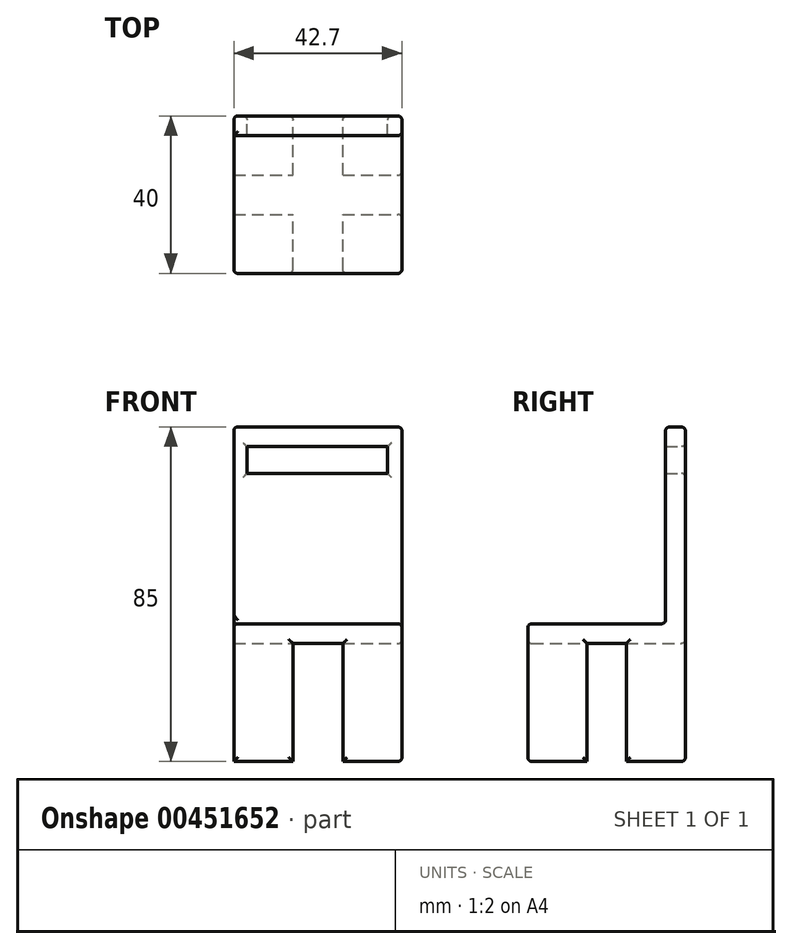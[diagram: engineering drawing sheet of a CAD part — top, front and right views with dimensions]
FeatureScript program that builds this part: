
annotation { "Feature Type Name" : "Feature", "Feature Type Description" : "" }
export const myFeature = defineFeature(function(context is Context, id is Id, definition is map)
    precondition{}
    {
        {
            var Q0;
            Q0=qCreatedBy(makeId("Top.planeOp"),FACE);
            var sketch = newSketch(context, id + "F0", { "sketchPlane" : qUnion([Q0])});
            skLineSegment(sketch, "E0.bottom", {"start": v(10, 10) * mm, "end": v(25, 10) * mm});
            skLineSegment(sketch, "E0.top", {"start": v(10, 25) * mm, "end": v(25, 25) * mm});
            skLineSegment(sketch, "E0.left", {"start": v(10, 10) * mm, "end": v(10, 25) * mm});
            skLineSegment(sketch, "E0.right", {"start": v(25, 10) * mm, "end": v(25, 25) * mm});
            skLineSegment(sketch, "E1.0.1.0", {"start": v(10, 50) * mm, "end": v(25, 50) * mm});
            skLineSegment(sketch, "E1.0.1.1", {"start": v(10, 35) * mm, "end": v(10, 50) * mm});
            skLineSegment(sketch, "E1.0.1.2", {"start": v(10, 35) * mm, "end": v(25, 35) * mm});
            skLineSegment(sketch, "E1.0.1.3", {"start": v(25, 35) * mm, "end": v(25, 50) * mm});
            skLineSegment(sketch, "E1.1.0.0", {"start": v(37.7, 25) * mm, "end": v(52.7, 25) * mm});
            skLineSegment(sketch, "E1.1.0.1", {"start": v(37.7, 10) * mm, "end": v(37.7, 25) * mm});
            skLineSegment(sketch, "E1.1.0.2", {"start": v(37.7, 10) * mm, "end": v(52.7, 10) * mm});
            skLineSegment(sketch, "E1.1.0.3", {"start": v(52.7, 10) * mm, "end": v(52.7, 25) * mm});
            skLineSegment(sketch, "E1.1.1.0", {"start": v(37.7, 50) * mm, "end": v(52.7, 50) * mm});
            skLineSegment(sketch, "E1.1.1.1", {"start": v(37.7, 35) * mm, "end": v(37.7, 50) * mm});
            skLineSegment(sketch, "E1.1.1.2", {"start": v(37.7, 35) * mm, "end": v(52.7, 35) * mm});
            skLineSegment(sketch, "E1.1.1.3", {"start": v(52.7, 35) * mm, "end": v(52.7, 50) * mm});
            skLineSegment(sketch, "E1.direction1", {"start": v(10, 25) * mm, "end": v(37.7, 25) * mm, "construction": true});
            skLineSegment(sketch, "E1.direction2", {"start": v(10, 25) * mm, "end": v(10, 50) * mm, "construction": true});
            skSolve(sketch);
        }
        {
            var Q0;
            Q0 = qSketchRegion(id + "F0", true);
            extrude(context, id + "F1", {"entities" : qUnion([Q0]), "depth" : 30 * mm});
        }
        {
            var Q0;
            Q0=makeQuery(id+"F1.opExtrude","CAP_FACE",FACE,{"disambiguationData":[OSD([sQuery(id+"F0.wireOp",EDGE,"E1.0.1.0"),sQuery(id+"F0.wireOp",EDGE,"E1.0.1.1"),sQuery(id+"F0.wireOp",EDGE,"E1.0.1.2"),sQuery(id+"F0.wireOp",EDGE,"E1.0.1.3")])],"isStart":false});
            var sketch = newSketch(context, id + "F2", { "sketchPlane" : qUnion([Q0])});
            skLineSegment(sketch, "E2.bottom", {"start": v(10, 50) * mm, "end": v(52.7, 50) * mm});
            skLineSegment(sketch, "E2.top", {"start": v(10, 10) * mm, "end": v(52.7, 10) * mm});
            skLineSegment(sketch, "E2.left", {"start": v(10, 50) * mm, "end": v(10, 10) * mm});
            skLineSegment(sketch, "E2.right", {"start": v(52.7, 50) * mm, "end": v(52.7, 10) * mm});
            skSolve(sketch);
        }
        {
            var Q0;
            Q0 = qSketchRegion(id + "F2", true);
            extrude(context, id + "F3", {"entities" : qUnion([Q0]), "operationType" : NewBodyOperationType.ADD, "depth" : 5 * mm});
        }
        {
            var Q0;
            Q0=makeQuery(id+"F3.opExtrude","CAP_FACE",FACE,{"disambiguationData":[OSD([sQuery(id+"F2.wireOp",EDGE,"E2.bottom"),sQuery(id+"F2.wireOp",EDGE,"E2.top"),sQuery(id+"F2.wireOp",EDGE,"E2.left"),sQuery(id+"F2.wireOp",EDGE,"E2.right")])],"isStart":false});
            var sketch = newSketch(context, id + "F4", { "sketchPlane" : qUnion([Q0])});
            skLineSegment(sketch, "E3.bottom", {"start": v(10, 50) * mm, "end": v(52.7, 50) * mm});
            skLineSegment(sketch, "E3.top", {"start": v(10, 45) * mm, "end": v(52.7, 45) * mm});
            skLineSegment(sketch, "E3.left", {"start": v(10, 50) * mm, "end": v(10, 45) * mm});
            skLineSegment(sketch, "E3.right", {"start": v(52.7, 50) * mm, "end": v(52.7, 45) * mm});
            skSolve(sketch);
        }
        {
            var Q0;
            Q0 = qSketchRegion(id + "F4", true);
            extrude(context, id + "F5", {"entities" : qUnion([Q0]), "operationType" : NewBodyOperationType.ADD, "depth" : 50 * mm});
        }
        {
            var Q0;
            Q0=makeQuery(id+"F5.boolean.opBoolean","MERGE",FACE,{"derivedFrom":[makeQuery(id+"F3.boolean.opBoolean","MERGE",FACE,{"derivedFrom":[makeQuery(id+"F1.opExtrude","SWEPT_FACE",FACE,{"disambiguationData":[OSD([sQuery(id+"F0.wireOp",EDGE,"E1.0.1.0")])]}),makeQuery(id+"F1.opExtrude","SWEPT_FACE",FACE,{"disambiguationData":[OSD([sQuery(id+"F0.wireOp",EDGE,"E1.1.1.0")])]}),makeQuery(id+"F3.opExtrude","SWEPT_FACE",FACE,{"disambiguationData":[OSD([sQuery(id+"F2.wireOp",EDGE,"E2.bottom")])]})]}),makeQuery(id+"F5.opExtrude","SWEPT_FACE",FACE,{"disambiguationData":[OSD([sQuery(id+"F4.wireOp",EDGE,"E3.bottom")])]})]});
            var sketch = newSketch(context, id + "F6", { "sketchPlane" : qUnion([Q0])});
            skLineSegment(sketch, "E4.bottom", {"start": v(-49.03, 79.97) * mm, "end": v(-13.33, 79.97) * mm});
            skLineSegment(sketch, "E4.top", {"start": v(-49.03, 73.2) * mm, "end": v(-13.33, 73.2) * mm});
            skLineSegment(sketch, "E4.left", {"start": v(-49.03, 79.97) * mm, "end": v(-49.03, 73.2) * mm});
            skLineSegment(sketch, "E4.right", {"start": v(-13.33, 79.97) * mm, "end": v(-13.33, 73.2) * mm});
            skSolve(sketch);
        }
        {
            var Q0;
            Q0 = qSketchRegion(id + "F6", true);
            extrude(context, id + "F7", {"entities" : qUnion([Q0]), "operationType" : NewBodyOperationType.REMOVE, "oppositeDirection" : true, "depth" : 25 * mm});
        }
        {
            var Q0;
            Q0=makeQuery(id+"F3.opExtrude","CAP_FACE",FACE,{"disambiguationData":[OSD([sQuery(id+"F2.wireOp",EDGE,"E2.bottom"),sQuery(id+"F2.wireOp",EDGE,"E2.top"),sQuery(id+"F2.wireOp",EDGE,"E2.left"),sQuery(id+"F2.wireOp",EDGE,"E2.right")])],"isStart":false});
            var Q1;
            Q1=makeQuery(id+"F5.opExtrude","CAP_FACE",FACE,{"disambiguationData":[OSD([sQuery(id+"F4.wireOp",EDGE,"E3.bottom"),sQuery(id+"F4.wireOp",EDGE,"E3.top"),sQuery(id+"F4.wireOp",EDGE,"E3.left"),sQuery(id+"F4.wireOp",EDGE,"E3.right")])],"isStart":false});
            var Q2;
            Q2=makeQuery(id+"F3.boolean.opBoolean","MERGE",FACE,{"derivedFrom":[makeQuery(id+"F1.opExtrude","SWEPT_FACE",FACE,{"disambiguationData":[OSD([sQuery(id+"F0.wireOp",EDGE,"E0.bottom")])]}),makeQuery(id+"F1.opExtrude","SWEPT_FACE",FACE,{"disambiguationData":[OSD([sQuery(id+"F0.wireOp",EDGE,"E1.1.0.2")])]}),makeQuery(id+"F3.opExtrude","SWEPT_FACE",FACE,{"disambiguationData":[OSD([sQuery(id+"F2.wireOp",EDGE,"E2.top")])]})]});
            var Q3;
            Q3=makeQuery(id+"F5.boolean.opBoolean","MERGE",FACE,{"derivedFrom":[makeQuery(id+"F3.boolean.opBoolean","MERGE",FACE,{"derivedFrom":[makeQuery(id+"F1.opExtrude","SWEPT_FACE",FACE,{"disambiguationData":[OSD([sQuery(id+"F0.wireOp",EDGE,"E1.1.0.3")])]}),makeQuery(id+"F1.opExtrude","SWEPT_FACE",FACE,{"disambiguationData":[OSD([sQuery(id+"F0.wireOp",EDGE,"E1.1.1.3")])]}),makeQuery(id+"F3.opExtrude","SWEPT_FACE",FACE,{"disambiguationData":[OSD([sQuery(id+"F2.wireOp",EDGE,"E2.right")])]})]}),makeQuery(id+"F5.opExtrude","SWEPT_FACE",FACE,{"disambiguationData":[OSD([sQuery(id+"F4.wireOp",EDGE,"E3.right")])]})]});
            var Q4;
            Q4=makeQuery(id+"F5.boolean.opBoolean","MERGE",EDGE,{"derivedFrom":[makeQuery(id+"F3.boolean.opBoolean","MERGE",EDGE,{"derivedFrom":[makeQuery(id+"F1.opExtrude","SWEPT_EDGE",EDGE,{"disambiguationData":[OSD([sQuery(id+"F0.wireOp",EDGE,"E1.1.1.0"),sQuery(id+"F0.wireOp",EDGE,"E1.1.1.3")])]}),makeQuery(id+"F3.opExtrude","SWEPT_EDGE",EDGE,{"disambiguationData":[OSD([sQuery(id+"F2.wireOp",EDGE,"E2.bottom"),sQuery(id+"F2.wireOp",EDGE,"E2.right")])]})]}),makeQuery(id+"F5.opExtrude","SWEPT_EDGE",EDGE,{"disambiguationData":[OSD([sQuery(id+"F4.wireOp",EDGE,"E3.bottom"),sQuery(id+"F4.wireOp",EDGE,"E3.right")])]})]});
            var Q5;
            Q5=makeQuery(id+"F5.boolean.opBoolean","MERGE",FACE,{"derivedFrom":[makeQuery(id+"F3.boolean.opBoolean","MERGE",FACE,{"derivedFrom":[makeQuery(id+"F1.opExtrude","SWEPT_FACE",FACE,{"disambiguationData":[OSD([sQuery(id+"F0.wireOp",EDGE,"E1.0.1.0")])]}),makeQuery(id+"F1.opExtrude","SWEPT_FACE",FACE,{"disambiguationData":[OSD([sQuery(id+"F0.wireOp",EDGE,"E1.1.1.0")])]}),makeQuery(id+"F3.opExtrude","SWEPT_FACE",FACE,{"disambiguationData":[OSD([sQuery(id+"F2.wireOp",EDGE,"E2.bottom")])]})]}),makeQuery(id+"F5.opExtrude","SWEPT_FACE",FACE,{"disambiguationData":[OSD([sQuery(id+"F4.wireOp",EDGE,"E3.bottom")])]})]});
            fillet(context, id + "F8", {"entities" : qUnion([Q0, Q1, Q2, Q3, Q4, Q5]), "radius" : 1 * mm, "tangentPropagation" : true, "allowEdgeOverflow" : false});
        }
    });
